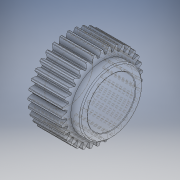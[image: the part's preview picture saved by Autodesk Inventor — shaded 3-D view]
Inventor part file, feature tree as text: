
AUTODESK INVENTOR PART (.ipt)
format: ipt  version: 2018 (Build 220112000, 112)  size: 611,840 bytes
history: native  units: mm
features: extrude x2, sketch x1, fillet x1, chamfer x1
ambient origin geometry x8: Origin, YZ Plane, XZ Plane, XY Plane, X Axis, Y Axis, Z Axis, Center Point
bodies: Solid1 (feature_tree)
feature tree (5):
  sketch  "Sketch1"  dims[d0=10.0mm d1=16.98mm d2=14.74mm d3=13.0mm d4=5.25mm d5=0.2mm d6=0.13mm d7=0.61mm d8=330.0mm d10=360.0deg d12=7.0mm d13=0.0mm d14=2.0mm d15=0.0mm d16=0.1mm d17=0.25mm d18=2.0mm d19=45.0deg]
  extrude  "Extrusion1"  Depth=2.0mm
  extrude  "Extrusion2"  Depth=2.0mm
  fillet  "Fillet1"  Radius=5.25mm
  chamfer  "Chamfer1"  Distance=0.2mm
